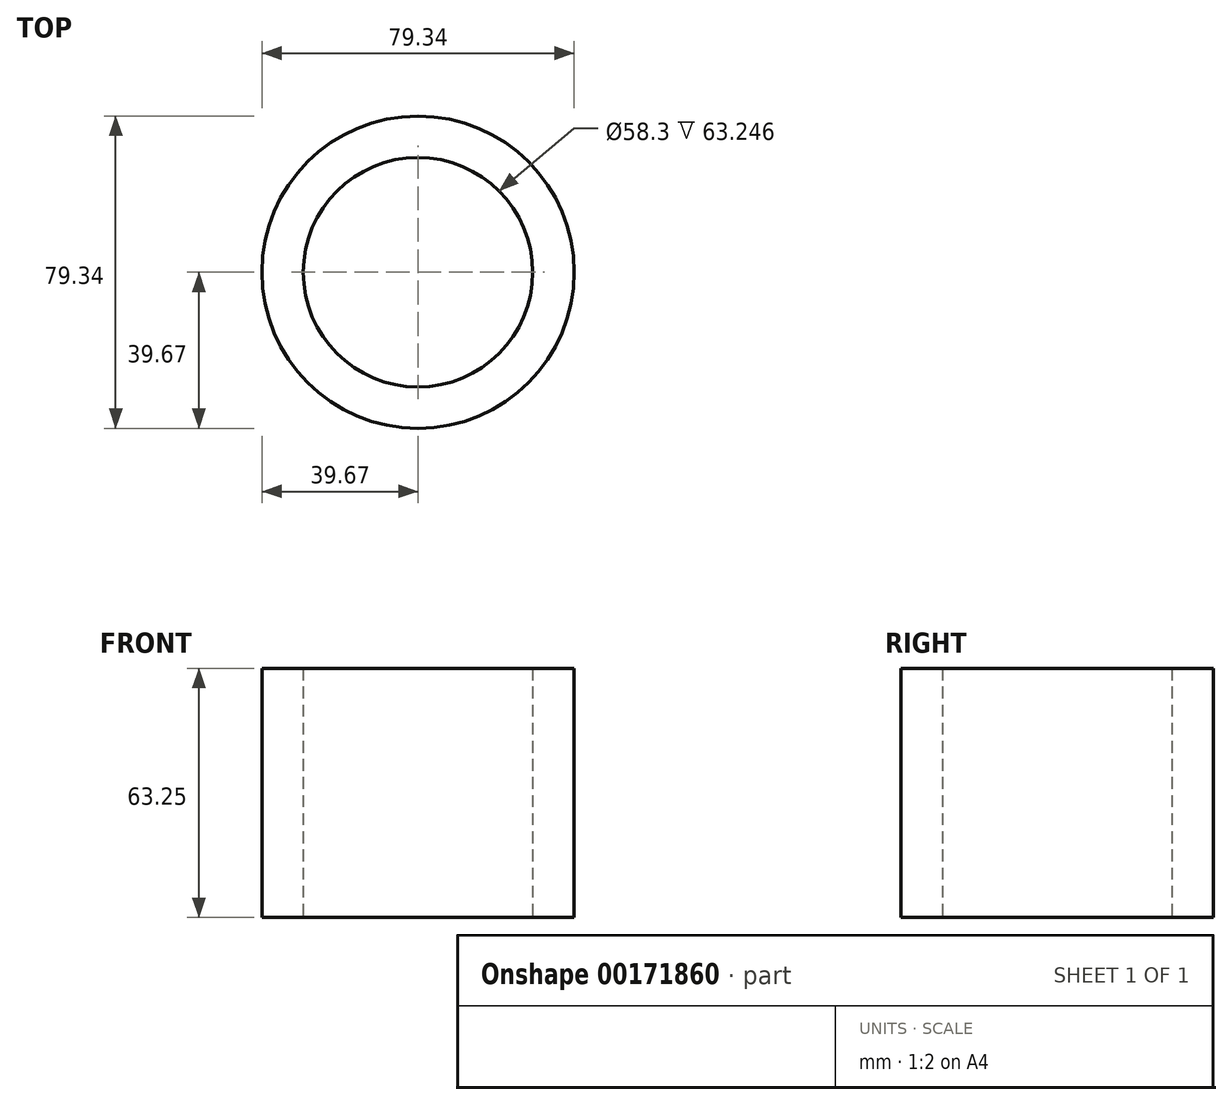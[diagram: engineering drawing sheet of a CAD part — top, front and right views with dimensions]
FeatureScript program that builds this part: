
annotation { "Feature Type Name" : "Feature", "Feature Type Description" : "" }
export const myFeature = defineFeature(function(context is Context, id is Id, definition is map)
    precondition{}
    {
        {
            var Q0;
            Q0=qCreatedBy(makeId("Top.planeOp"),FACE);
            var sketch = newSketch(context, id + "F0", { "sketchPlane" : qUnion([Q0])});
            skCircle(sketch, "E0", {"center": v(0, 0) * mm, "radius": 39.67 * mm});
            skCircle(sketch, "E1", {"center": v(0, 0) * mm, "radius": 29.15 * mm});
            skSolve(sketch);
        }
        {
            var Q0;
            Q0=makeQuery(id+"F0.imprint","IMPRINT",FACE,{"disambiguationData":[TD([[makeQuery(id+"F0.imprint","IMPRINT",EDGE,{"derivedFrom":sQuery(id+"F0.wireOp",EDGE,"E0")}),1.0]])]});
            extrude(context, id + "F1", {"entities" : qUnion([Q0]), "depth" : 63.25 * mm});
        }
    });
